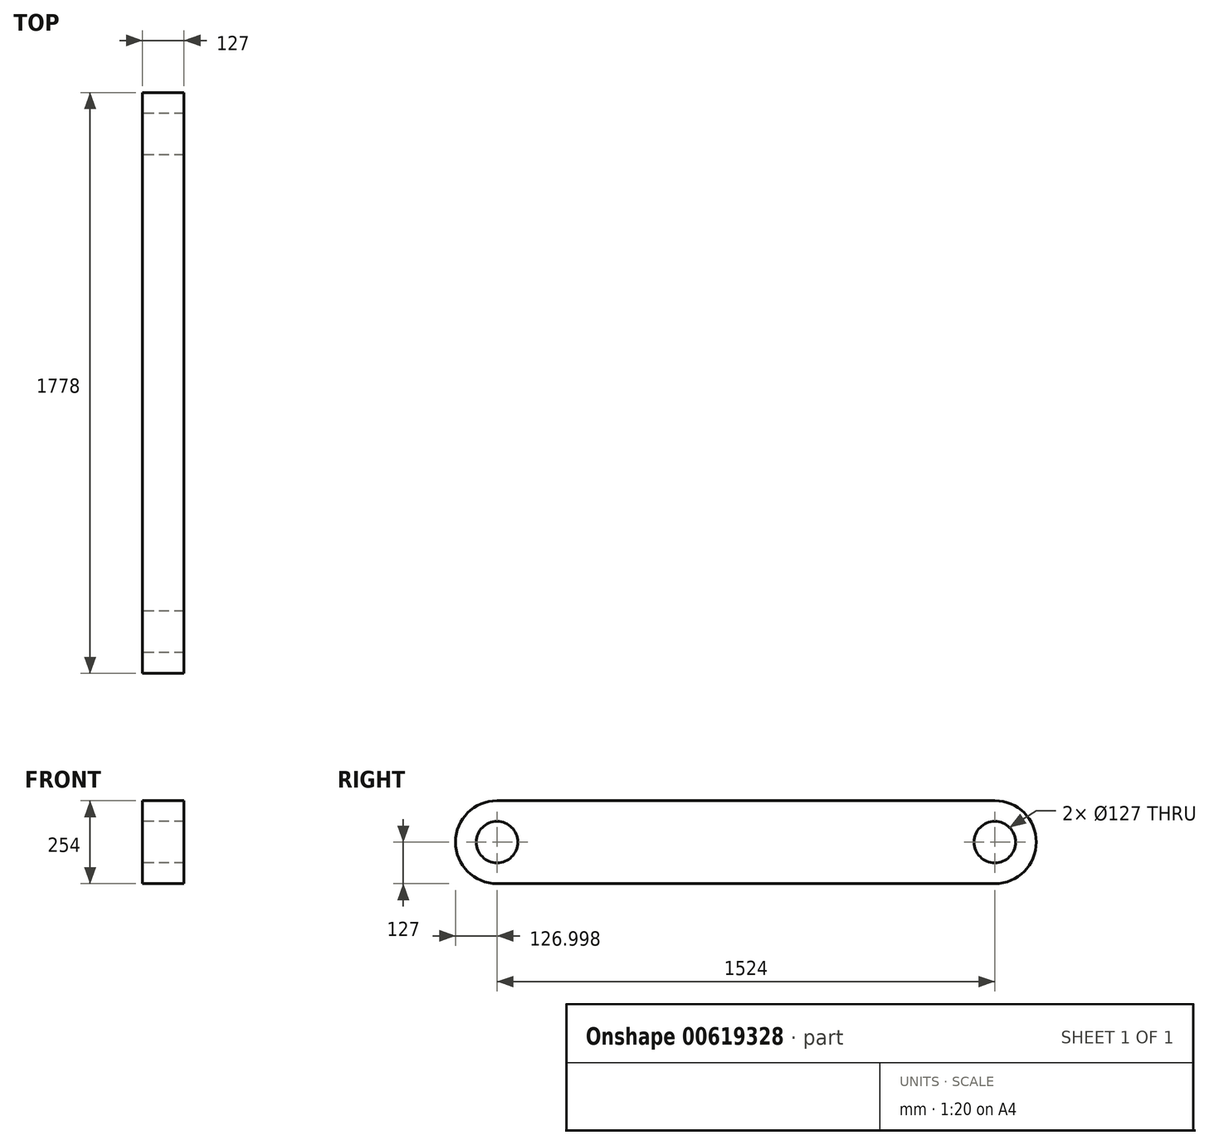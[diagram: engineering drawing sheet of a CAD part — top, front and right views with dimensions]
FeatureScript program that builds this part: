
annotation { "Feature Type Name" : "Feature", "Feature Type Description" : "" }
export const myFeature = defineFeature(function(context is Context, id is Id, definition is map)
    precondition{}
    {
        {
            var Q0;
            Q0=qCreatedBy(makeId("Right.planeOp"),FACE);
            var sketch = newSketch(context, id + "F0", { "sketchPlane" : qUnion([Q0])});
            skArc(sketch, "E0", {"start": v(-1100.07, 127) * mm, "mid": v(-1227.07, 0) * mm, "end": v(-1100.07, -127) * mm});
            skArc(sketch, "E1", {"start": v(423.93, -127) * mm, "mid": v(550.93, 0) * mm, "end": v(423.93, 127) * mm});
            skLineSegment(sketch, "E2", {"start": v(-1100.07, 127) * mm, "end": v(423.93, 127) * mm});
            skLineSegment(sketch, "E3", {"start": v(-1100.07, -127) * mm, "end": v(423.93, -127) * mm});
            skCircle(sketch, "E4", {"center": v(-1100.07, 0) * mm, "radius": 63.5 * mm});
            skCircle(sketch, "E5", {"center": v(423.93, 0) * mm, "radius": 63.5 * mm});
            skSolve(sketch);
        }
        {
            var Q0;
            Q0 = qSketchRegion(id + "F0", true);
            extrude(context, id + "F1", {"entities" : qUnion([Q0]), "depth" : 127 * mm, "offsetDistance" : 25.4 * mm});
        }
    });
